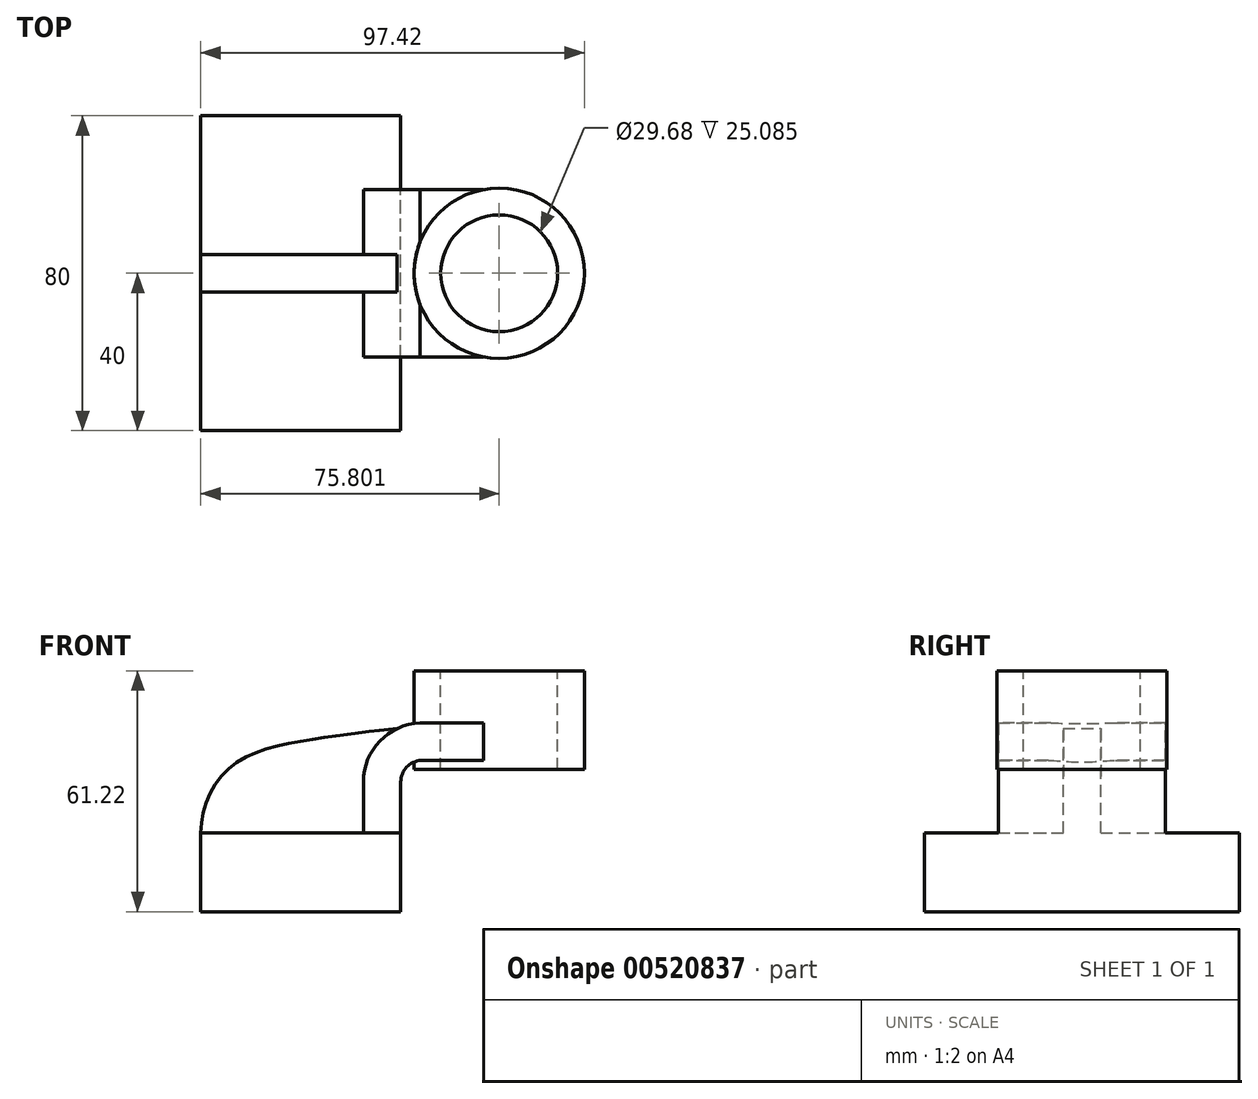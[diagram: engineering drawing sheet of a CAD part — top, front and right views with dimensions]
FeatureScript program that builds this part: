
annotation { "Feature Type Name" : "Feature", "Feature Type Description" : "" }
export const myFeature = defineFeature(function(context is Context, id is Id, definition is map)
    precondition{}
    {
        {
            var Q0;
            Q0=qCreatedBy(makeId("Front.planeOp"),FACE);
            var sketch = newSketch(context, id + "F0", { "sketchPlane" : qUnion([Q0])});
            skLineSegment(sketch, "E0.bottom", {"start": v(0, 20) * mm, "end": v(50.8, 20) * mm});
            skLineSegment(sketch, "E0.top", {"start": v(0, 0) * mm, "end": v(50.8, 0) * mm});
            skLineSegment(sketch, "E0.left", {"start": v(0, 20) * mm, "end": v(0, 0) * mm});
            skLineSegment(sketch, "E0.right", {"start": v(50.8, 20) * mm, "end": v(50.8, 0) * mm});
            skLineSegment(sketch, "E1.bottom", {"start": v(59.38, 61) * mm, "end": v(90.69, 61) * mm});
            skLineSegment(sketch, "E1.top", {"start": v(59.38, 36.21) * mm, "end": v(90.69, 36.21) * mm});
            skLineSegment(sketch, "E1.left", {"start": v(59.38, 61) * mm, "end": v(59.38, 36.21) * mm});
            skLineSegment(sketch, "E1.right", {"start": v(90.69, 61) * mm, "end": v(90.69, 36.21) * mm});
            skLineSegment(sketch, "E2", {"start": v(50.8, 20) * mm, "end": v(50.8, 32.97) * mm});
            skArc(sketch, "E3", {"start": v(50.8, 32.97) * mm, "mid": v(52.28, 36.72) * mm, "end": v(55.93, 38.45) * mm});
            skLineSegment(sketch, "E4", {"start": v(55.93, 38.45) * mm, "end": v(76.03, 38.45) * mm});
            skLineSegment(sketch, "E5.0", {"start": v(55.7, 47.95) * mm, "end": v(76.03, 47.95) * mm});
            skArc(sketch, "E5.1", {"start": v(41.3, 32.97) * mm, "mid": v(45.48, 43.36) * mm, "end": v(55.7, 47.95) * mm});
            skLineSegment(sketch, "E5.2", {"start": v(41.3, 20) * mm, "end": v(41.3, 32.97) * mm});
            skPoint(sketch, "E6.1.internal.snap0", {"position": v(52.28, 36.72) * mm});
            skFitSpline(sketch, "E6", {"points": [v(0, 20) * mm, v(7.5, 36.72) * mm, v(29.22, 43.9) * mm, v(49.9, 46.53) * mm], "startDerivative": vector(0, 58.53) * mm, "endDerivative": vector(47.28, 3.3) * mm});
            skLineSegment(sketch, "E7", {"start": v(76.03, 47.95) * mm, "end": v(76.03, 38.45) * mm});
            skSolve(sketch);
        }
        {
            var Q0;
            Q0=makeQuery(id+"F0.imprint","IMPRINT",FACE,{"disambiguationData":[TD([[makeQuery(id+"F0.imprint","IMPRINT",EDGE,{"derivedFrom":sQuery(id+"F0.wireOp",EDGE,"E0.top")}),1.0]])]});
            extrude(context, id + "F1", {"entities" : qUnion([Q0]), "endBound" : BoundingType.SYMMETRIC, "depth" : 80 * mm});
        }
        {
            var Q0;
            {var subQ1=sQuery(id+"F0.wireOp",EDGE,"E2");Q0=makeQuery(id+"F0.imprint","IMPRINT",FACE,{"disambiguationData":[TD([[makeQuery(id+"F0.imprint","IMPRINT",EDGE,{"derivedFrom":subQ1}),1.0]])]});}
            var Q1;
            {var subQ5=sQuery(id+"F0.wireOp",EDGE,"E7");Q1=makeQuery(id+"F0.imprint","IMPRINT",FACE,{"disambiguationData":[TD([[makeQuery(id+"F0.imprint","IMPRINT",EDGE,{"derivedFrom":subQ5}),-1.0]])]});}
            extrude(context, id + "F2", {"entities" : qUnion([Q0, Q1]), "operationType" : NewBodyOperationType.ADD, "endBound" : BoundingType.SYMMETRIC, "depth" : 42.5 * mm});
        }
        {
            var Q0;
            {var subQ2=sQuery(id+"F0.wireOp",EDGE,"E5.2");Q0=makeQuery(id+"F0.imprint","IMPRINT",FACE,{"disambiguationData":[TD([[makeQuery(id+"F0.imprint","IMPRINT",EDGE,{"derivedFrom":subQ2}),1.0]])]});}
            extrude(context, id + "F3", {"entities" : qUnion([Q0]), "operationType" : NewBodyOperationType.ADD, "endBound" : BoundingType.SYMMETRIC, "depth" : 9.5 * mm});
        }
        {
            var Q0;
            Q0=qCreatedBy(makeId("Front.planeOp"),FACE);
            var sketch = newSketch(context, id + "F4", { "sketchPlane" : qUnion([Q0])});
            skLineSegment(sketch, "E8.bottom", {"start": v(54.18, 61.22) * mm, "end": v(75.8, 61.22) * mm});
            skLineSegment(sketch, "E8.top", {"start": v(54.18, 36.13) * mm, "end": v(75.8, 36.13) * mm});
            skLineSegment(sketch, "E8.left", {"start": v(54.18, 61.22) * mm, "end": v(54.18, 36.13) * mm});
            skLineSegment(sketch, "E8.right", {"start": v(75.8, 61.22) * mm, "end": v(75.8, 36.13) * mm});
            skSolve(sketch);
        }
        {
            var Q0;
            Q0 = qSketchRegion(id + "F4", true);
            var Q1;
            Q1=sQuery(id+"F4.wireOp",EDGE,"E8.right");
            revolve(context, id + "F5", {"operationType" : NewBodyOperationType.ADD, "entities" : qUnion([Q0]), "axis" : qUnion([Q1]), "revolveType" : RevolveType.FULL});
        }
        {
            var Q0;
            Q0=makeQuery(id+"F5.opRevolve","SWEPT_FACE",FACE,{"disambiguationData":[OSD([sQuery(id+"F4.wireOp",EDGE,"E8.bottom")])]});
            var sketch = newSketch(context, id + "F6", { "sketchPlane" : qUnion([Q0])});
            skCircle(sketch, "E9", {"center": v(75.8, 0) * mm, "radius": 14.84 * mm});
            skSolve(sketch);
        }
        {
            var Q0;
            Q0 = qSketchRegion(id + "F6", true);
            extrude(context, id + "F7", {"entities" : qUnion([Q0]), "operationType" : NewBodyOperationType.REMOVE, "endBound" : BoundingType.THROUGH_ALL, "oppositeDirection" : true, "depth" : 25 * mm});
        }
    });
